# Revit family: Door lintel try (bb2)
name_source: partatom
category: Doors
units: mm (PartAtom-declared; Revit-internal decimal feet)

## family parameters
Always vertical = Yes
Cut with Voids When Loaded = No
Host = Wall
OmniClass Number = 23.30.10.00
OmniClass Title = Doors
Room Calculation Point = No
Shared = No

## types (7) — shared parameters
Frame Material = <By Category>
Frame Offset = 0' - 2"
Frame Projection Ext. = 0' - 1"
Frame Projection Int. = 0' - 1"
Frame Width = 0' - 3"
Function = Interior
Height = 7' - 0"
Lintel Material = <By Category>
Panel Length = 6' - 10 1/4"
Panel Material = <By Category>
Sunshade depth on both side = 0' - 4"
Thickness = 0' - 1 1/2"
Wall Closure = By host
sunshade length = 0' - 4"

## per-type parameters (varying)
| type | SL | Width |
| Hausplus Door 3'-4" | 4' - 0" | 3' - 4" |
| Hausplus Door 3'-0" | 3' - 8" | 3' - 0" |
| Hausplus Door 2'-6" | 3' - 2" | 2' - 6" |
| Hausplus Door 2'-0" | 2' - 8" | 2' - 0" |
| Hausplus Door 3'-6" | 4' - 2" | 3' - 6" |
| Hausplus Door 3'-9" | 4' - 5" | 3' - 9" |
| Hausplus Door 4'-0" | 5' - 8" | 5' - 0" |

## geometry (parser evidence)
native form markers: Sweep x18
no freeform markers — native parametric forms only
